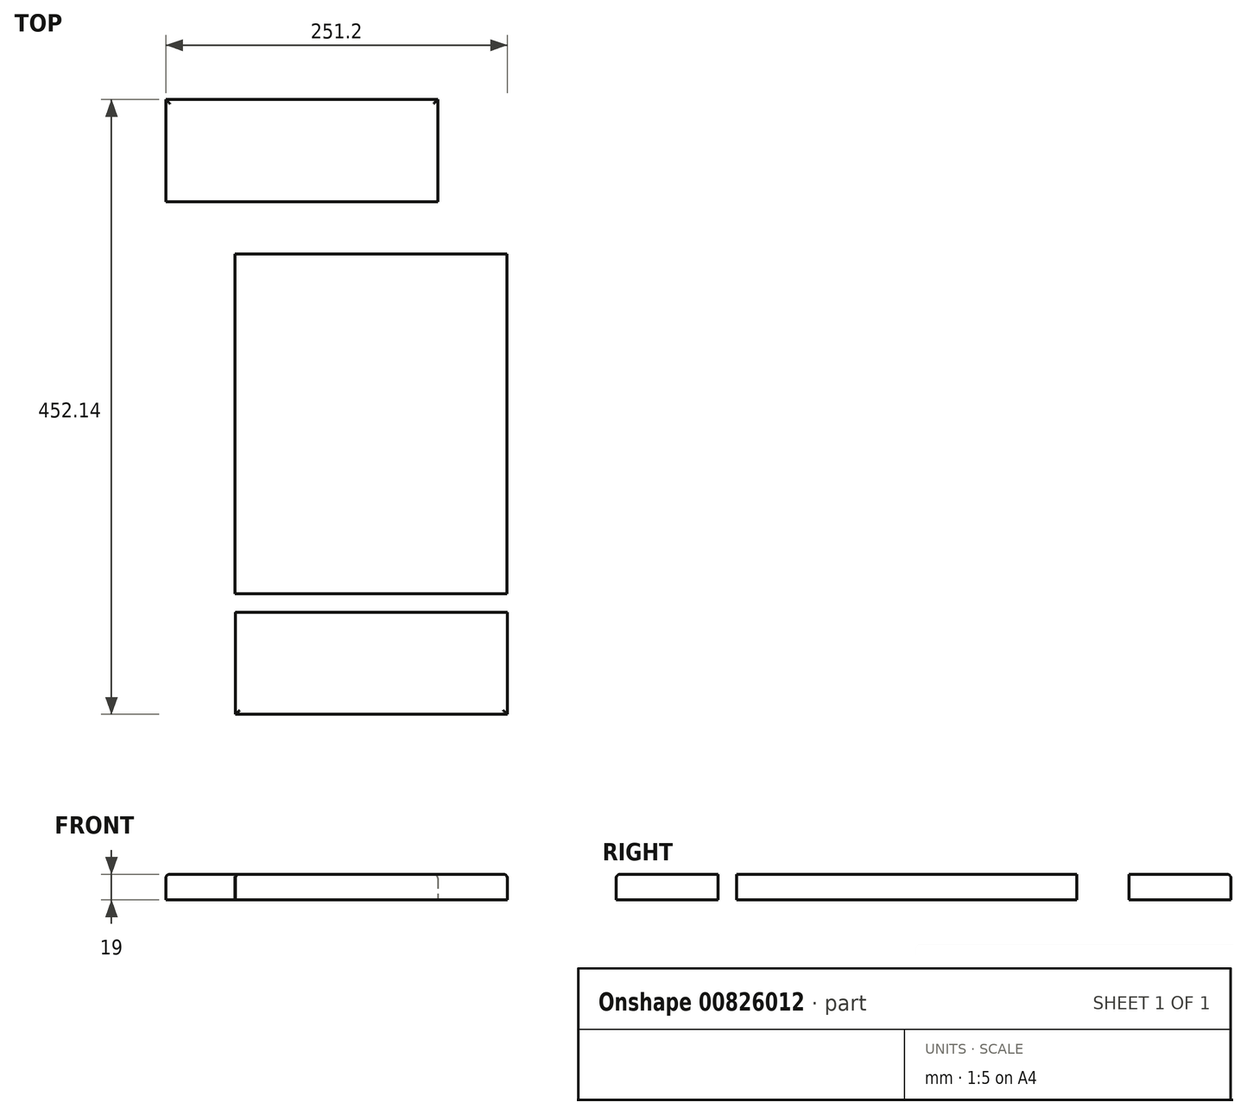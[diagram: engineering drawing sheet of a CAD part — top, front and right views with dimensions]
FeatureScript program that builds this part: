
annotation { "Feature Type Name" : "Feature", "Feature Type Description" : "" }
export const myFeature = defineFeature(function(context is Context, id is Id, definition is map)
    precondition{}
    {
        {
            var Q0;
            Q0=qCreatedBy(makeId("Top.planeOp"),FACE);
            var sketch = newSketch(context, id + "F0", { "sketchPlane" : qUnion([Q0])});
            skLineSegment(sketch, "E0.bottom", {"start": v(-154.88, 107.86) * mm, "end": v(45.12, 107.86) * mm});
            skLineSegment(sketch, "E0.top", {"start": v(-154.88, -142.14) * mm, "end": v(45.12, -142.14) * mm});
            skLineSegment(sketch, "E0.left", {"start": v(-154.88, 107.86) * mm, "end": v(-154.88, -142.14) * mm});
            skLineSegment(sketch, "E0.right", {"start": v(45.12, 107.86) * mm, "end": v(45.12, -142.14) * mm});
            skSolve(sketch);
        }
        {
            var Q0;
            Q0=qCreatedBy(makeId("Top.planeOp"),FACE);
            var sketch = newSketch(context, id + "F1", { "sketchPlane" : qUnion([Q0])});
            skLineSegment(sketch, "E1.bottom", {"start": v(-154.43, -155.75) * mm, "end": v(45.57, -155.75) * mm});
            skLineSegment(sketch, "E1.top", {"start": v(-154.43, -230.75) * mm, "end": v(45.57, -230.75) * mm});
            skLineSegment(sketch, "E1.left", {"start": v(-154.43, -155.75) * mm, "end": v(-154.43, -230.75) * mm});
            skLineSegment(sketch, "E1.right", {"start": v(45.57, -155.75) * mm, "end": v(45.57, -230.75) * mm});
            skSolve(sketch);
        }
        {
            var Q0;
            Q0=qCreatedBy(makeId("Top.planeOp"),FACE);
            var sketch = newSketch(context, id + "F2", { "sketchPlane" : qUnion([Q0])});
            skLineSegment(sketch, "E2.bottom", {"start": v(-205.63, 146.39) * mm, "end": v(-5.63, 146.39) * mm});
            skLineSegment(sketch, "E2.top", {"start": v(-205.63, 221.39) * mm, "end": v(-5.63, 221.39) * mm});
            skLineSegment(sketch, "E2.left", {"start": v(-205.63, 146.39) * mm, "end": v(-205.63, 221.39) * mm});
            skLineSegment(sketch, "E2.right", {"start": v(-5.63, 146.39) * mm, "end": v(-5.63, 221.39) * mm});
            skSolve(sketch);
        }
        {
            var Q0;
            Q0 = qSketchRegion(id + "F0", true);
            extrude(context, id + "F3", {"entities" : qUnion([Q0]), "depth" : 19 * mm, "offsetDistance" : 25 * mm});
        }
        {
            var Q0;
            Q0 = qSketchRegion(id + "F1", true);
            extrude(context, id + "F4", {"entities" : qUnion([Q0]), "depth" : 19 * mm, "offsetDistance" : 25 * mm});
        }
        {
            var Q0;
            Q0 = qSketchRegion(id + "F2", true);
            extrude(context, id + "F5", {"entities" : qUnion([Q0]), "depth" : 19 * mm, "offsetDistance" : 25 * mm});
        }
        {
            var Q0;
            Q0=makeQuery(id+"F5.opExtrude","CAP_EDGE",EDGE,{"disambiguationData":[OSD([sQuery(id+"F2.wireOp",EDGE,"E2.left")])],"isStart":false});
            var Q1;
            Q1=makeQuery(id+"F5.opExtrude","CAP_EDGE",EDGE,{"disambiguationData":[OSD([sQuery(id+"F2.wireOp",EDGE,"E2.top")])],"isStart":false});
            var Q2;
            Q2=makeQuery(id+"F5.opExtrude","CAP_EDGE",EDGE,{"disambiguationData":[OSD([sQuery(id+"F2.wireOp",EDGE,"E2.right")])],"isStart":false});
            var Q3;
            Q3=makeQuery(id+"F3.opExtrude","CAP_EDGE",EDGE,{"disambiguationData":[OSD([sQuery(id+"F0.wireOp",EDGE,"E0.right")])],"isStart":false});
            var Q4;
            Q4=makeQuery(id+"F3.opExtrude","CAP_EDGE",EDGE,{"disambiguationData":[OSD([sQuery(id+"F0.wireOp",EDGE,"E0.left")])],"isStart":false});
            var Q5;
            Q5=makeQuery(id+"F4.opExtrude","CAP_EDGE",EDGE,{"disambiguationData":[OSD([sQuery(id+"F1.wireOp",EDGE,"E1.left")])],"isStart":false});
            var Q6;
            Q6=makeQuery(id+"F4.opExtrude","CAP_EDGE",EDGE,{"disambiguationData":[OSD([sQuery(id+"F1.wireOp",EDGE,"E1.top")])],"isStart":false});
            var Q7;
            Q7=makeQuery(id+"F4.opExtrude","CAP_EDGE",EDGE,{"disambiguationData":[OSD([sQuery(id+"F1.wireOp",EDGE,"E1.right")])],"isStart":false});
            fillet(context, id + "F6", {"entities" : qUnion([Q0, Q1, Q2, Q3, Q4, Q5, Q6, Q7]), "radius" : 3 * mm, "tangentPropagation" : true, "allowEdgeOverflow" : false});
        }
    });
